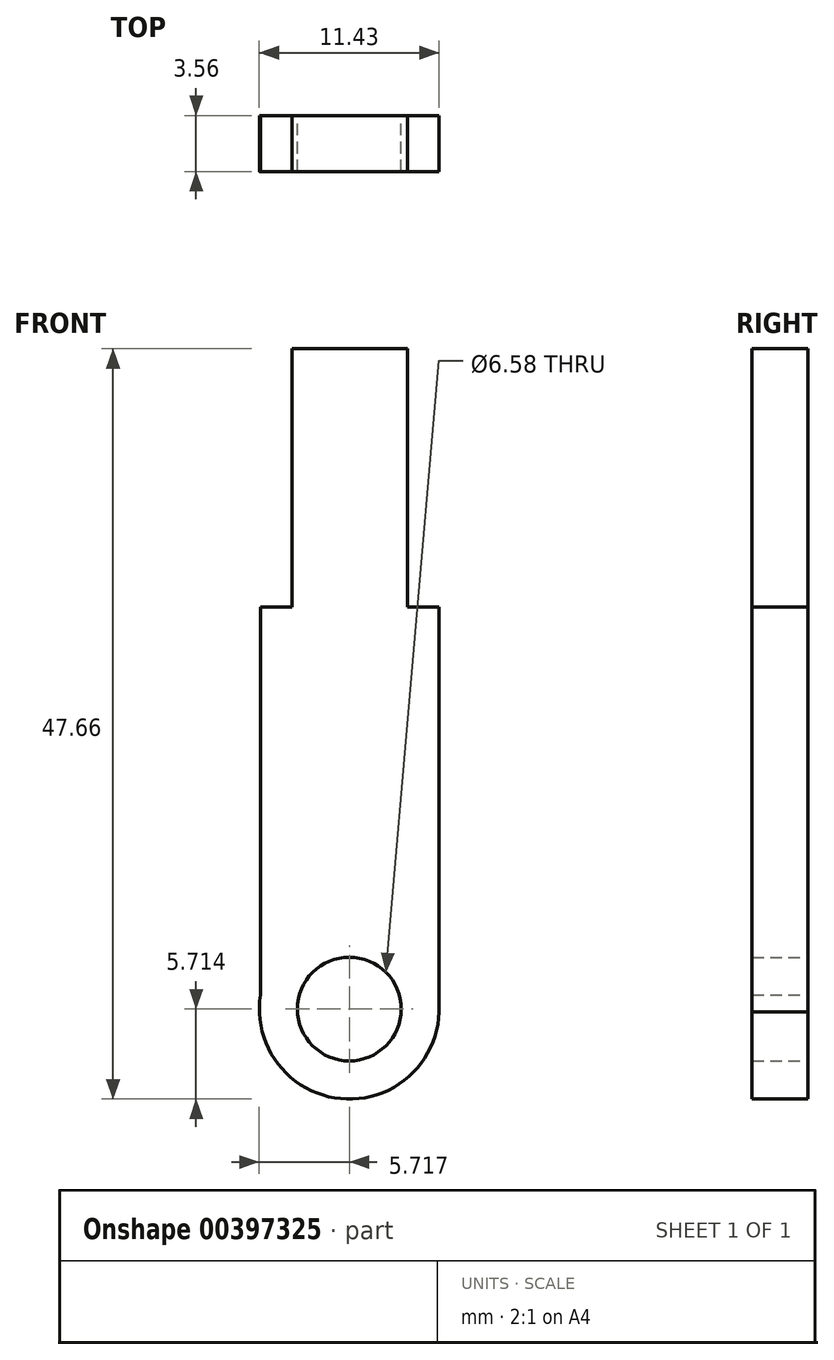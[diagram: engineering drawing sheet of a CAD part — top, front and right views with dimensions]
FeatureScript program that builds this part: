
annotation { "Feature Type Name" : "Feature", "Feature Type Description" : "" }
export const myFeature = defineFeature(function(context is Context, id is Id, definition is map)
    precondition{}
    {
        {
            var Q0;
            Q0=qCreatedBy(makeId("Front.planeOp"),FACE);
            var sketch = newSketch(context, id + "F0", { "sketchPlane" : qUnion([Q0])});
            skCircle(sketch, "E0", {"center": v(31.02, -28.73) * mm, "radius": 3.3 * mm});
            skCircle(sketch, "E1", {"center": v(31.02, -28.73) * mm, "radius": 5.71 * mm});
            skLineSegment(sketch, "E2.bottom", {"start": v(36.73, -28.91) * mm, "end": v(25.38, -28.91) * mm});
            skLineSegment(sketch, "E2.top", {"start": v(36.73, -3.17) * mm, "end": v(25.38, -3.17) * mm});
            skLineSegment(sketch, "E2.left", {"start": v(36.73, -28.91) * mm, "end": v(36.73, -3.17) * mm});
            skLineSegment(sketch, "E2.right", {"start": v(25.38, -28.91) * mm, "end": v(25.38, -3.17) * mm});
            skLineSegment(sketch, "E3.bottom", {"start": v(34.72, 13.22) * mm, "end": v(27.39, 13.22) * mm});
            skLineSegment(sketch, "E3.top", {"start": v(34.72, -19.56) * mm, "end": v(27.39, -19.56) * mm});
            skLineSegment(sketch, "E3.left", {"start": v(34.72, 13.22) * mm, "end": v(34.72, -19.56) * mm});
            skLineSegment(sketch, "E3.right", {"start": v(27.39, 13.22) * mm, "end": v(27.39, -19.56) * mm});
            skPoint(sketch, "E3.middle", {"position": v(31.05, -3.17) * mm});
            skSolve(sketch);
        }
        {
            var Q0;
            {var subQ5=sQuery(id+"F0.wireOp",EDGE,"E3.bottom");Q0=makeQuery(id+"F0.imprint","IMPRINT",FACE,{"disambiguationData":[TD([[makeQuery(id+"F0.imprint","IMPRINT",EDGE,{"derivedFrom":subQ5}),1.0]])]});}
            var Q1;
            {var subQ5=sQuery(id+"F0.wireOp",EDGE,"E3.top");Q1=makeQuery(id+"F0.imprint","IMPRINT",FACE,{"disambiguationData":[TD([[makeQuery(id+"F0.imprint","IMPRINT",EDGE,{"derivedFrom":subQ5}),-1.0]])]});}
            var Q2;
            {var subQ12=sQuery(id+"F0.wireOp",EDGE,"E3.top");Q2=makeQuery(id+"F0.imprint","IMPRINT",FACE,{"disambiguationData":[TD([[makeQuery(id+"F0.imprint","IMPRINT",EDGE,{"derivedFrom":subQ12}),1.0]])]});}
            var Q3;
            {var subQ1=sQuery(id+"F0.wireOp",EDGE,"E2.bottom");var subQ4=sQuery(id+"F0.wireOp",EDGE,"E0");var subQ5=makeQuery(id+"F0.imprint","INTERSECT",VERTEX,{"disambiguationData":[OD(0.0)],"derivedFrom":[subQ4,subQ1]});Q3=makeQuery(id+"F0.imprint","IMPRINT",FACE,{"disambiguationData":[TD([[makeQuery(id+"F0.imprint","IMPRINT",EDGE,{"disambiguationData":[TD([[subQ5,-1.0]])],"derivedFrom":subQ4}),-1.0]])]});}
            var Q4;
            {var subQ1=sQuery(id+"F0.wireOp",EDGE,"E2.bottom");var subQ3=sQuery(id+"F0.wireOp",EDGE,"E0");var subQ8=makeQuery(id+"F0.imprint","INTERSECT",VERTEX,{"disambiguationData":[OD(0.0)],"derivedFrom":[subQ3,subQ1]});Q4=makeQuery(id+"F0.imprint","IMPRINT",FACE,{"disambiguationData":[TD([[makeQuery(id+"F0.imprint","IMPRINT",EDGE,{"disambiguationData":[TD([[subQ8,1.0]])],"derivedFrom":subQ3}),-1.0]])]});}
            extrude(context, id + "F1", {"entities" : qUnion([Q0, Q1, Q2, Q3, Q4]), "depth" : 3.56 * mm});
        }
    });
